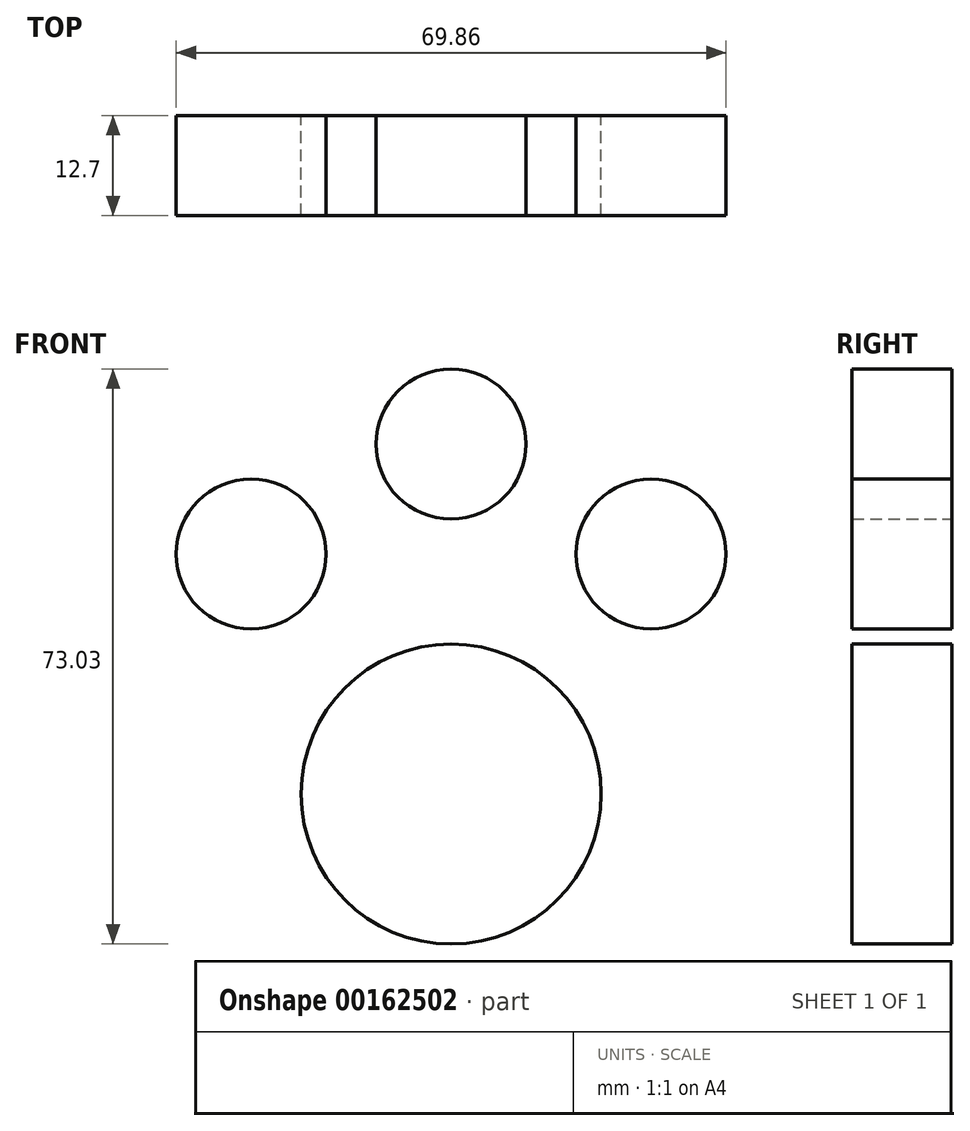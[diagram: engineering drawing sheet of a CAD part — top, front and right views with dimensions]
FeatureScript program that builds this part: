
annotation { "Feature Type Name" : "Feature", "Feature Type Description" : "" }
export const myFeature = defineFeature(function(context is Context, id is Id, definition is map)
    precondition{}
    {
        {
            var Q0;
            Q0=qCreatedBy(makeId("Front.planeOp"),FACE);
            var sketch = newSketch(context, id + "F0", { "sketchPlane" : qUnion([Q0])});
            skCircle(sketch, "E0", {"center": v(0, 0) * mm, "radius": 19.05 * mm});
            skCircle(sketch, "E1", {"center": v(-25.4, 30.48) * mm, "radius": 9.53 * mm});
            skCircle(sketch, "E2", {"center": v(0, 44.45) * mm, "radius": 9.53 * mm});
            skCircle(sketch, "E3", {"center": v(25.4, 30.48) * mm, "radius": 9.53 * mm});
            skSolve(sketch);
        }
        {
            var Q0;
            Q0 = qSketchRegion(id + "F0", true);
            extrude(context, id + "F1", {"entities" : qUnion([Q0]), "depth" : 12.7 * mm, "offsetDistance" : 25.4 * mm});
        }
    });
